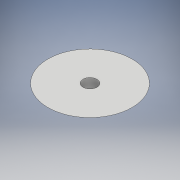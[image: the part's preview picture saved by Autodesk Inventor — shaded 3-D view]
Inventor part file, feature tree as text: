
AUTODESK INVENTOR PART (.ipt)
format: ipt  version: 2017 (Build 210142000, 142)  size: 100,864 bytes
history: native  units: mm
features: sketch x2, revolve x1, extrude x1
ambient origin geometry x8: Origin, YZ Plane, XZ Plane, XY Plane, X Axis, Y Axis, Z Axis, Center Point
bodies: Body1 (feature_tree)
feature tree (4):
  revolve  "Revolution1"  [1 undecoded]
  extrude  "Extrusion2"  Depth=10.0mm
  sketch  "Sketch1"  dims[d3=30.0mm d4=10.0mm]
  sketch  "Sketch2"  dims[d5=90.0deg d6=10.0mm d7=10.0mm d8=0.0mm]
note: 1 required parameter value undecoded (feature->parameter linkage not recoverable at this tier; creation-order binding heuristic only, values carry confidence <= 0.55)
